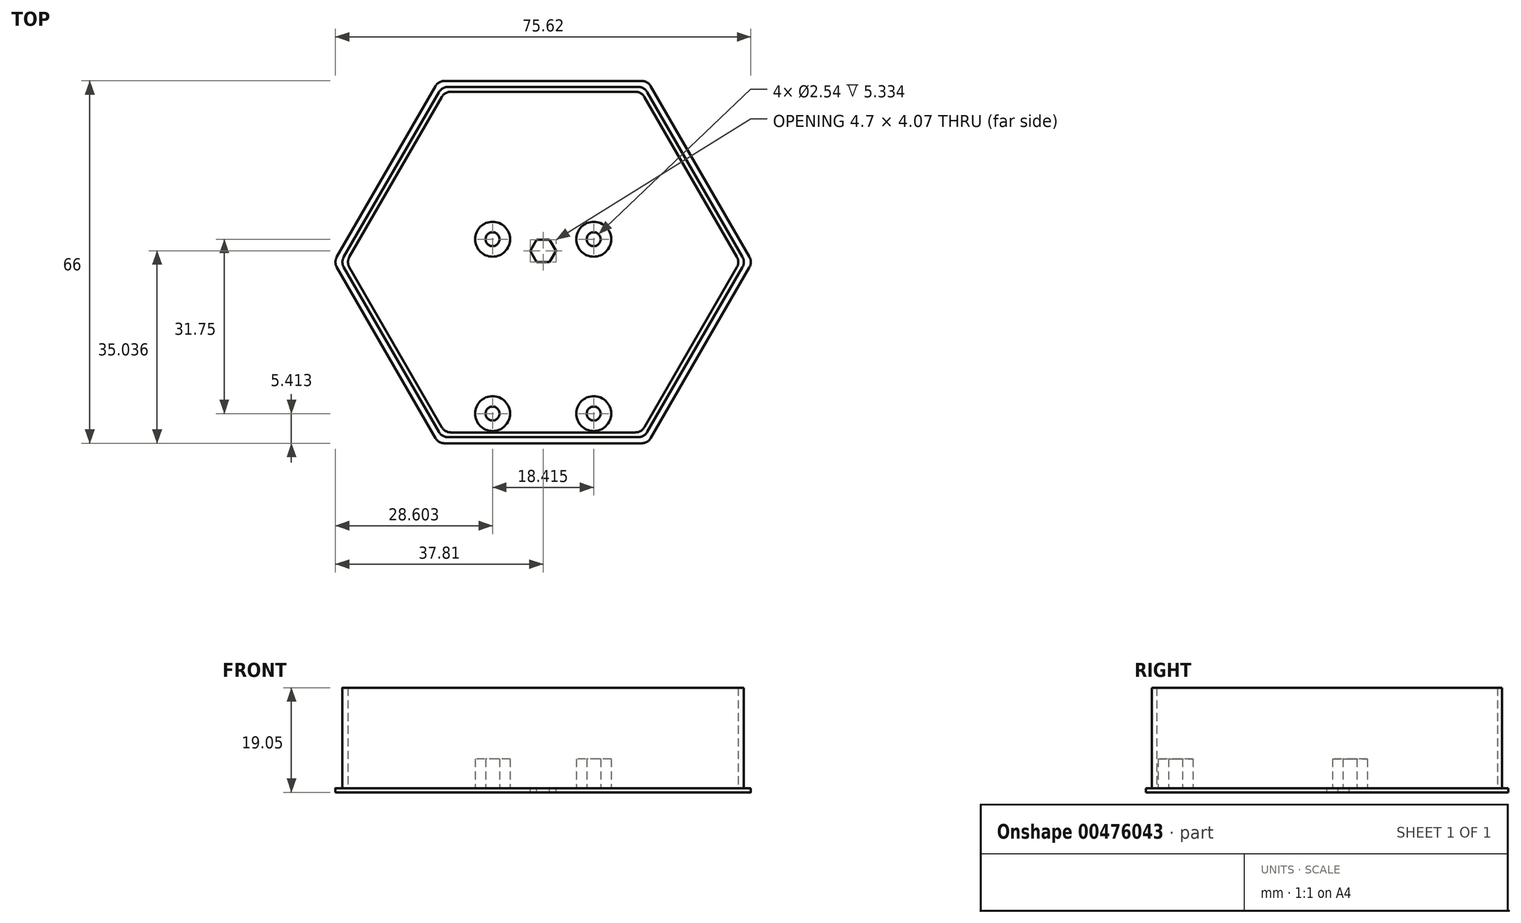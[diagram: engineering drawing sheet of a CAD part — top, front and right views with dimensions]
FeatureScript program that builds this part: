
annotation { "Feature Type Name" : "Feature", "Feature Type Description" : "" }
export const myFeature = defineFeature(function(context is Context, id is Id, definition is map)
    precondition{}
    {
        {
            var Q0;
            Q0=qCreatedBy(makeId("Top.planeOp"),FACE);
            var sketch = newSketch(context, id + "F0", { "sketchPlane" : qUnion([Q0])});
            skLineSegment(sketch, "E0", {"start": v(-56.1, -68.55) * mm, "end": v(58.07, -68.55) * mm});
            skLineSegment(sketch, "E1", {"start": v(0, 0) * mm, "end": v(-19.05, 33) * mm, "construction": true});
            skLineSegment(sketch, "E2", {"start": v(19.05, 33) * mm, "end": v(0, 0) * mm, "construction": true});
            skLineSegment(sketch, "E3", {"start": v(-19.05, 33) * mm, "end": v(19.05, 33) * mm});
            skLineSegment(sketch, "E4.1.0", {"start": v(-38.1, 0) * mm, "end": v(-19.05, 33) * mm});
            skLineSegment(sketch, "E4.2.0", {"start": v(-19.05, -33) * mm, "end": v(-38.1, 0) * mm});
            skLineSegment(sketch, "E4.3.0", {"start": v(19.05, -33) * mm, "end": v(-19.05, -33) * mm});
            skLineSegment(sketch, "E4.4.0", {"start": v(38.1, 0) * mm, "end": v(19.05, -33) * mm});
            skLineSegment(sketch, "E4.5.0", {"start": v(19.05, 33) * mm, "end": v(38.1, 0) * mm});
            skPoint(sketch, "E4.center", {"position": v(0, 0) * mm});
            skSolve(sketch);
        }
        {
            var Q0;
            Q0=makeQuery(id+"F0.imprint","IMPRINT",FACE,{"disambiguationData":[TD([[makeQuery(id+"F0.imprint","IMPRINT",EDGE,{"derivedFrom":sQuery(id+"F0.wireOp",EDGE,"E3")}),-1.0]])]});
            extrude(context, id + "F1", {"entities" : qUnion([Q0]), "depth" : 0.76 * mm, "offsetDistance" : 25.4 * mm});
        }
        {
            var Q0;
            Q0=makeQuery(id+"FdZoSmRdGPEDfu0_1.splitOp","SPLIT",EDGE,{"derivedFrom":makeQuery(id+"F1.opExtrude","SWEPT_EDGE",EDGE,{"disambiguationData":[OSD([sQuery(id+"F0.wireOp",EDGE,"E4.4.0"),sQuery(id+"F0.wireOp",EDGE,"E4.5.0")])]})});
            var Q1;
            Q1=makeQuery(id+"FdZoSmRdGPEDfu0_1.splitOp","SPLIT",EDGE,{"derivedFrom":makeQuery(id+"F1.opExtrude","SWEPT_EDGE",EDGE,{"disambiguationData":[OSD([sQuery(id+"F0.wireOp",EDGE,"E3"),sQuery(id+"F0.wireOp",EDGE,"E4.5.0")])]})});
            var Q2;
            Q2=makeQuery(id+"FdZoSmRdGPEDfu0_1.splitOp","SPLIT",EDGE,{"derivedFrom":makeQuery(id+"F1.opExtrude","SWEPT_EDGE",EDGE,{"disambiguationData":[OSD([sQuery(id+"F0.wireOp",EDGE,"E3"),sQuery(id+"F0.wireOp",EDGE,"E4.1.0")])]})});
            var Q3;
            Q3=makeQuery(id+"FdZoSmRdGPEDfu0_1.splitOp","SPLIT",EDGE,{"derivedFrom":makeQuery(id+"F1.opExtrude","SWEPT_EDGE",EDGE,{"disambiguationData":[OSD([sQuery(id+"F0.wireOp",EDGE,"E4.1.0"),sQuery(id+"F0.wireOp",EDGE,"E4.2.0")])]})});
            var Q4;
            Q4=makeQuery(id+"FdZoSmRdGPEDfu0_1.splitOp","SPLIT",EDGE,{"derivedFrom":makeQuery(id+"F1.opExtrude","SWEPT_EDGE",EDGE,{"disambiguationData":[OSD([sQuery(id+"F0.wireOp",EDGE,"E4.2.0"),sQuery(id+"F0.wireOp",EDGE,"E4.3.0")])]})});
            var Q5;
            Q5=makeQuery(id+"FdZoSmRdGPEDfu0_1.splitOp","SPLIT",EDGE,{"derivedFrom":makeQuery(id+"F1.opExtrude","SWEPT_EDGE",EDGE,{"disambiguationData":[OSD([sQuery(id+"F0.wireOp",EDGE,"E4.3.0"),sQuery(id+"F0.wireOp",EDGE,"E4.4.0")])]})});
            fillet(context, id + "F2", {"entities" : qUnion([Q0, Q1, Q2, Q3, Q4, Q5]), "radius" : 1.9 * mm, "allowEdgeOverflow" : false});
        }
        {
            var Q0;
            Q0=qCreatedBy(makeId("Top.planeOp"),FACE);
            var sketch = newSketch(context, id + "F3", { "sketchPlane" : qUnion([Q0])});
            skLineSegment(sketch, "E5", {"start": v(0, 0) * mm, "end": v(-18.41, 31.9) * mm, "construction": true});
            skLineSegment(sketch, "E6", {"start": v(0, 0) * mm, "end": v(18.41, 31.9) * mm, "construction": true});
            skLineSegment(sketch, "E7", {"start": v(-18.41, 31.9) * mm, "end": v(18.41, 31.9) * mm});
            skLineSegment(sketch, "E8.1.0", {"start": v(-36.83, 0) * mm, "end": v(-18.41, 31.9) * mm});
            skLineSegment(sketch, "E8.2.0", {"start": v(-18.42, -31.9) * mm, "end": v(-36.83, 0) * mm});
            skLineSegment(sketch, "E8.3.0", {"start": v(18.41, -31.9) * mm, "end": v(-18.41, -31.9) * mm});
            skLineSegment(sketch, "E8.4.0", {"start": v(36.83, 0) * mm, "end": v(18.41, -31.9) * mm});
            skLineSegment(sketch, "E8.5.0", {"start": v(18.41, 31.9) * mm, "end": v(36.83, 0) * mm});
            skPoint(sketch, "E8.center", {"position": v(0, 0) * mm});
            skSolve(sketch);
        }
        {
            var Q0;
            Q0=qSketchRegion(id+"F3",true);
            extrude(context, id + "F4", {"entities" : qUnion([Q0]), "depth" : 19.05 * mm, "offsetDistance" : 25.4 * mm});
        }
        {
            var Q0;
            Q0=makeQuery(id+"F4.opExtrude","SWEPT_EDGE",EDGE,{"disambiguationData":[OSD([sQuery(id+"F3.wireOp",EDGE,"E8.2.0"),sQuery(id+"F3.wireOp",EDGE,"E8.3.0")])]});
            var Q1;
            Q1=makeQuery(id+"F4.opExtrude","SWEPT_EDGE",EDGE,{"disambiguationData":[OSD([sQuery(id+"F3.wireOp",EDGE,"E8.3.0"),sQuery(id+"F3.wireOp",EDGE,"E8.4.0")])]});
            var Q2;
            Q2=makeQuery(id+"F4.opExtrude","SWEPT_EDGE",EDGE,{"disambiguationData":[OSD([sQuery(id+"F3.wireOp",EDGE,"E8.4.0"),sQuery(id+"F3.wireOp",EDGE,"E8.5.0")])]});
            var Q3;
            Q3=makeQuery(id+"F4.opExtrude","SWEPT_EDGE",EDGE,{"disambiguationData":[OSD([sQuery(id+"F3.wireOp",EDGE,"E8.1.0"),sQuery(id+"F3.wireOp",EDGE,"E8.2.0")])]});
            var Q4;
            Q4=makeQuery(id+"F4.opExtrude","SWEPT_EDGE",EDGE,{"disambiguationData":[OSD([sQuery(id+"F3.wireOp",EDGE,"E7"),sQuery(id+"F3.wireOp",EDGE,"E8.5.0")])]});
            var Q5;
            Q5=makeQuery(id+"F4.opExtrude","SWEPT_EDGE",EDGE,{"disambiguationData":[OSD([sQuery(id+"F3.wireOp",EDGE,"E7"),sQuery(id+"F3.wireOp",EDGE,"E8.1.0")])]});
            fillet(context, id + "F5", {"entities" : qUnion([Q0, Q1, Q2, Q3, Q4, Q5]), "radius" : 1.9 * mm, "tangentPropagation" : true, "allowEdgeOverflow" : false});
        }
        {
            var Q0;
            Q0=qCreatedBy(makeId("Top.planeOp"),FACE);
            var sketch = newSketch(context, id + "F6", { "sketchPlane" : qUnion([Q0])});
            skLineSegment(sketch, "E9", {"start": v(-17.9, 31.02) * mm, "end": v(0, 0) * mm, "construction": true});
            skLineSegment(sketch, "E10", {"start": v(0, 0) * mm, "end": v(17.9, 31.02) * mm, "construction": true});
            skLineSegment(sketch, "E11", {"start": v(-17.9, 31.02) * mm, "end": v(17.9, 31.02) * mm});
            skLineSegment(sketch, "E12.1.0", {"start": v(-35.81, 0) * mm, "end": v(-17.9, 31.02) * mm});
            skLineSegment(sketch, "E12.2.0", {"start": v(-17.9, -31.02) * mm, "end": v(-35.81, 0) * mm});
            skLineSegment(sketch, "E12.3.0", {"start": v(17.9, -31.02) * mm, "end": v(-17.9, -31.02) * mm});
            skLineSegment(sketch, "E12.4.0", {"start": v(35.81, 0) * mm, "end": v(17.9, -31.02) * mm});
            skLineSegment(sketch, "E12.5.0", {"start": v(17.9, 31.02) * mm, "end": v(35.81, 0) * mm});
            skPoint(sketch, "E12.center", {"position": v(0, 0) * mm});
            skSolve(sketch);
        }
        {
            var Q0;
            Q0 = qSketchRegion(id + "F6", true);
            extrude(context, id + "F7", {"entities" : qUnion([Q0]), "depth" : 25.4 * mm, "offsetDistance" : 25.4 * mm});
        }
        {
            var Q0;
            Q0=makeQuery(id+"F7.opExtrude","SWEPT_EDGE",EDGE,{"disambiguationData":[OSD([sQuery(id+"F6.wireOp",EDGE,"E12.2.0"),sQuery(id+"F6.wireOp",EDGE,"E12.3.0")])]});
            var Q1;
            Q1=makeQuery(id+"F7.opExtrude","SWEPT_EDGE",EDGE,{"disambiguationData":[OSD([sQuery(id+"F6.wireOp",EDGE,"E12.3.0"),sQuery(id+"F6.wireOp",EDGE,"E12.4.0")])]});
            var Q2;
            Q2=makeQuery(id+"F7.opExtrude","SWEPT_EDGE",EDGE,{"disambiguationData":[OSD([sQuery(id+"F6.wireOp",EDGE,"E12.4.0"),sQuery(id+"F6.wireOp",EDGE,"E12.5.0")])]});
            var Q3;
            Q3=makeQuery(id+"F7.opExtrude","SWEPT_EDGE",EDGE,{"disambiguationData":[OSD([sQuery(id+"F6.wireOp",EDGE,"E12.1.0"),sQuery(id+"F6.wireOp",EDGE,"E12.2.0")])]});
            var Q4;
            Q4=makeQuery(id+"F7.opExtrude","SWEPT_EDGE",EDGE,{"disambiguationData":[OSD([sQuery(id+"F6.wireOp",EDGE,"E11"),sQuery(id+"F6.wireOp",EDGE,"E12.5.0")])]});
            var Q5;
            Q5=makeQuery(id+"F7.opExtrude","SWEPT_EDGE",EDGE,{"disambiguationData":[OSD([sQuery(id+"F6.wireOp",EDGE,"E11"),sQuery(id+"F6.wireOp",EDGE,"E12.1.0")])]});
            fillet(context, id + "F8", {"entities" : qUnion([Q0, Q1, Q2, Q3, Q4, Q5]), "radius" : 1.9 * mm, "tangentPropagation" : true, "allowEdgeOverflow" : false});
        }
        {
            var Q0;
            Q0=makeQuery(id+"F7.opExtrude","SWEPT_BODY",BODY,{"disambiguationData":[OSD([sQuery(id+"F6.wireOp",EDGE,"E11"),sQuery(id+"F6.wireOp",EDGE,"E12.1.0"),sQuery(id+"F6.wireOp",EDGE,"E12.2.0"),sQuery(id+"F6.wireOp",EDGE,"E12.3.0"),sQuery(id+"F6.wireOp",EDGE,"E12.4.0"),sQuery(id+"F6.wireOp",EDGE,"E12.5.0")])]});
            transform(context, id + "F9", {"entities" : qUnion([Q0]), "transformType" : TransformType.TRANSLATION_3D, "dx" : 0 * mm, "dy" : 0 * mm, "dz" : 0.76 * mm, "makeCopy" : false});
        }
        {
            var Q0;
            Q0=makeQuery(id+"F7.opExtrude","SWEPT_BODY",BODY,{"disambiguationData":[OSD([sQuery(id+"F6.wireOp",EDGE,"E11"),sQuery(id+"F6.wireOp",EDGE,"E12.1.0"),sQuery(id+"F6.wireOp",EDGE,"E12.2.0"),sQuery(id+"F6.wireOp",EDGE,"E12.3.0"),sQuery(id+"F6.wireOp",EDGE,"E12.4.0"),sQuery(id+"F6.wireOp",EDGE,"E12.5.0")])]});
            var Q1;
            Q1=makeQuery(id+"F4.opExtrude","SWEPT_BODY",BODY,{"disambiguationData":[OSD([sQuery(id+"F3.wireOp",EDGE,"E7"),sQuery(id+"F3.wireOp",EDGE,"E8.1.0"),sQuery(id+"F3.wireOp",EDGE,"E8.2.0"),sQuery(id+"F3.wireOp",EDGE,"E8.3.0"),sQuery(id+"F3.wireOp",EDGE,"E8.4.0"),sQuery(id+"F3.wireOp",EDGE,"E8.5.0")])]});
            booleanBodies(context, id + "F10", {"operationType" : BooleanOperationType.SUBTRACTION, "tools" : qUnion([Q0]), "targets" : qUnion([Q1])});
        }
        {
            var Q0;
            Q0=makeQuery(id+"F10.opBoolean","COPY",FACE,{"derivedFrom":makeQuery(id+"F7.opExtrude","CAP_FACE",FACE,{"disambiguationData":[OSD([sQuery(id+"F6.wireOp",EDGE,"E11"),sQuery(id+"F6.wireOp",EDGE,"E12.1.0"),sQuery(id+"F6.wireOp",EDGE,"E12.2.0"),sQuery(id+"F6.wireOp",EDGE,"E12.3.0"),sQuery(id+"F6.wireOp",EDGE,"E12.4.0"),sQuery(id+"F6.wireOp",EDGE,"E12.5.0")])],"isStart":true})});
            var sketch = newSketch(context, id + "F11", { "sketchPlane" : qUnion([Q0])});
            skLineSegment(sketch, "E13.bottom", {"start": v(-12.7, 7.6) * mm, "end": v(12.7, 7.6) * mm});
            skLineSegment(sketch, "E13.top", {"start": v(-12.7, -31.02) * mm, "end": v(12.7, -31.02) * mm});
            skLineSegment(sketch, "E13.left", {"start": v(-12.7, 7.6) * mm, "end": v(-12.7, -31.02) * mm});
            skLineSegment(sketch, "E13.right", {"start": v(12.7, 7.6) * mm, "end": v(12.7, -31.02) * mm});
            skPoint(sketch, "E14", {"position": v(0, 2.04) * mm});
            skCircle(sketch, "E15.cCircle", {"center": v(0, 2.04) * mm, "radius": 2.04 * mm, "construction": true});
            skLineSegment(sketch, "E15.0", {"start": v(1.18, 0) * mm, "end": v(-1.18, 0) * mm});
            skLineSegment(sketch, "E15.1", {"start": v(-1.18, 0) * mm, "end": v(-2.35, 2.04) * mm});
            skLineSegment(sketch, "E15.2", {"start": v(-2.35, 2.04) * mm, "end": v(-1.18, 4.07) * mm});
            skLineSegment(sketch, "E15.3", {"start": v(-1.18, 4.07) * mm, "end": v(1.18, 4.07) * mm});
            skLineSegment(sketch, "E15.4", {"start": v(1.18, 4.07) * mm, "end": v(2.35, 2.04) * mm});
            skLineSegment(sketch, "E15.5", {"start": v(2.35, 2.04) * mm, "end": v(1.18, 0) * mm});
            skPoint(sketch, "E15.0.midPoint", {"position": v(0, 0) * mm});
            skLineSegment(sketch, "E16", {"start": v(-12.7, -11.71) * mm, "end": v(12.7, -11.71) * mm, "construction": true});
            skLineSegment(sketch, "E17.bottom", {"start": v(9.2, 4.16) * mm, "end": v(-9.2, 4.16) * mm, "construction": true});
            skLineSegment(sketch, "E17.top", {"start": v(9.2, -27.59) * mm, "end": v(-9.2, -27.59) * mm, "construction": true});
            skLineSegment(sketch, "E17.left", {"start": v(9.2, 4.16) * mm, "end": v(9.2, -27.59) * mm, "construction": true});
            skLineSegment(sketch, "E17.right", {"start": v(-9.2, 4.16) * mm, "end": v(-9.2, -27.59) * mm, "construction": true});
            skPoint(sketch, "E17.middle", {"position": v(0, -11.71) * mm});
            skCircle(sketch, "E18", {"center": v(-9.2, 4.16) * mm, "radius": 3.18 * mm});
            skCircle(sketch, "E19", {"center": v(9.2, 4.16) * mm, "radius": 3.18 * mm});
            skCircle(sketch, "E20", {"center": v(-9.2, -27.59) * mm, "radius": 3.18 * mm});
            skCircle(sketch, "E21", {"center": v(9.2, -27.59) * mm, "radius": 3.18 * mm});
            skCircle(sketch, "E22", {"center": v(-9.2, 4.16) * mm, "radius": 1.27 * mm});
            skCircle(sketch, "E23", {"center": v(9.2, 4.16) * mm, "radius": 1.27 * mm});
            skCircle(sketch, "E24", {"center": v(-9.2, -27.59) * mm, "radius": 1.27 * mm});
            skCircle(sketch, "E25", {"center": v(9.2, -27.59) * mm, "radius": 1.27 * mm});
            skSolve(sketch);
        }
        {
            var Q0;
            Q0=makeQuery(id+"F11.imprint","IMPRINT",FACE,{"disambiguationData":[TD([[makeQuery(id+"F11.imprint","IMPRINT",EDGE,{"derivedFrom":sQuery(id+"F11.wireOp",EDGE,"E15.0")}),-1.0]])]});
            extrude(context, id + "F12", {"entities" : qUnion([Q0]), "operationType" : NewBodyOperationType.REMOVE, "oppositeDirection" : true, "depth" : 25.4 * mm, "offsetDistance" : 25.4 * mm});
        }
        {
            var Q0;
            Q0=makeQuery(id+"F11.imprint","IMPRINT",FACE,{"disambiguationData":[TD([[makeQuery(id+"F11.imprint","IMPRINT",EDGE,{"derivedFrom":sQuery(id+"F11.wireOp",EDGE,"E18")}),1.0]])]});
            var Q1;
            Q1=makeQuery(id+"F11.imprint","IMPRINT",FACE,{"disambiguationData":[TD([[makeQuery(id+"F11.imprint","IMPRINT",EDGE,{"derivedFrom":sQuery(id+"F11.wireOp",EDGE,"E19")}),1.0]])]});
            var Q2;
            Q2=makeQuery(id+"F11.imprint","IMPRINT",FACE,{"disambiguationData":[TD([[makeQuery(id+"F11.imprint","IMPRINT",EDGE,{"derivedFrom":sQuery(id+"F11.wireOp",EDGE,"E21")}),1.0]])]});
            var Q3;
            Q3=makeQuery(id+"F11.imprint","IMPRINT",FACE,{"disambiguationData":[TD([[makeQuery(id+"F11.imprint","IMPRINT",EDGE,{"derivedFrom":sQuery(id+"F11.wireOp",EDGE,"E20")}),1.0]])]});
            extrude(context, id + "F13", {"entities" : qUnion([Q0, Q1, Q2, Q3]), "operationType" : NewBodyOperationType.ADD, "depth" : 5.33 * mm, "offsetDistance" : 25.4 * mm});
        }
    });
